FCSTD DOCUMENT  (FreeCAD 0.15R4671 (Git))
Label: TopCornerIdler_III
License: All rights reserved
LicenseURL: http://en.wikipedia.org/wiki/All_rights_reserved
objects: Sketcher::SketchObject×18, PartDesign::Pocket×17, PartDesign::Fillet×12, Part::Feature×11, Mesh::Feature×9, PartDesign::Pad×1
note: 77 computed .brp shape members not serialized (recipe doc carries the construction recipe); baked Part::Feature solids carry a one-line shape summary decoded from their .brp

FEATURE [Part::Feature] Part__Feature  label="OB1515_45mm001"
  Placement = pos=(0,-20.5,22.5) rot=(1,0,0;1.5708rad)
  shape: bbox 15 x 45 x 15 mm, 158 faces (baked)
FEATURE [Part::Feature] Part__Feature001  label="OB1515_45mm002"
  Placement = pos=(20.5,0,22.5) rot=(0.57735,0.57735,0.57735;2.0944rad)
  shape: bbox 45 x 15 x 15 mm, 158 faces (baked)
FEATURE [Part::Feature] Part__Feature002  label="OB1515_45mm"
  Placement = pos=(7,-7,-15) rot=(0,0,1;0.785398rad)
  shape: bbox 21.01 x 21.01 x 45 mm, 158 faces (baked)
FEATURE [Sketcher::SketchObject] Sketch
  Placement = pos=(0,0,2) rot=(0,0,1;0rad)
  sketch-geometry (5):
    g0: LineSegment StartX=-7.5 StartY=7.5 StartZ=0 EndX=62.0538 EndY=7.5 EndZ=0
    g1: LineSegment StartX=62.0538 StartY=7.5 StartZ=0 EndX=62.0538 EndY=-59.9462 EndZ=0
    g2: LineSegment StartX=62.0538 StartY=-59.9462 StartZ=0 EndX=52.5 EndY=-69.5 EndZ=0
    g3: LineSegment StartX=52.5 StartY=-69.5 StartZ=0 EndX=-7.5 EndY=-69.5 EndZ=0
    g4: LineSegment StartX=-7.5 StartY=-69.5 StartZ=0 EndX=-7.5 EndY=7.5 EndZ=0
  constraints (12):
    c: Coincident(g0,g1)
    c: Coincident(g1,g2)
    c: Coincident(g2,g3)
    c: Coincident(g3,g4)
    c: Coincident(g4,g0)
    c: Horizontal(g3)
    c: Horizontal(g0)
    c: Vertical(g1)
    c: Vertical(g4)
    c: Angle(g2,g-2) = 0.785398
    c: DistanceX(g0) = -7.5
    c: DistanceY(g0) = 7.5
FEATURE [Part::Feature] Part__Feature003  label="NEMA17"
  Placement = pos=(36,-36,2) rot=(0,0,1;0rad)
  shape: bbox 42.3 x 42.3 x 68 mm, 275 faces (baked)
FEATURE [Part::Feature] Part__Feature004  label="T5_Pulley"
  Placement = pos=(36,-36,-4) rot=(0,0,1;0rad)
  shape: bbox 16 x 16 x 14.8 mm, 116 faces (baked)
FEATURE [Mesh::Feature] _mmRod_x100mm  label="8mmRod_x100mm"
  Placement = pos=(36,-145.5,-3.5) rot=(0,0,1;3.14159rad)
FEATURE [Mesh::Feature] _08ZZ_Ball_Bearing  label="608ZZ_Ball_Bearing"
  Placement = pos=(54.5,-36,14) rot=(0,0,1;0rad)
FEATURE [Mesh::Feature] _08ZZ_Ball_Bearing001  label="608ZZ_Ball_Bearing001"
  Placement = pos=(54.5,-36,25.1) rot=(0,0,1;0rad)
FEATURE [Mesh::Feature] Spacer
  Placement = pos=(21.5,-46,17.6) rot=(0,0,1;0rad)
FEATURE [Part::Feature] LM8UU_8mm_Linear_Bearing
  Placement = pos=(36,-99.5,-3.5) rot=(0,0,1;1.5708rad)
  shape: bbox 15 x 24 x 15 mm, 34 faces (baked)
FEATURE [PartDesign::Pad] Pad
  Length = 28
  Length2 = 100
  Placement = pos=(0,0,2) rot=(0,0,1;0rad)
  Sketch = -> Sketch
  Type = 0
FEATURE [Sketcher::SketchObject] Sketch001
  Placement = pos=(0,0,30) rot=(0,0,1;0rad)
  Support = -> Pad [Face7]
  sketch-geometry (5):
    g0: LineSegment StartX=14.5 StartY=-73.368 StartZ=0 EndX=14.5 EndY=-19.8192 EndZ=0
    g1: LineSegment StartX=14.5 StartY=-19.8192 StartZ=0 EndX=19.8192 EndY=-14.5 EndZ=0
    g2: LineSegment StartX=19.8192 StartY=-14.5 StartZ=0 EndX=77 EndY=-14.5 EndZ=0
    g3: LineSegment StartX=77 StartY=-14.5 StartZ=0 EndX=77 EndY=-73.368 EndZ=0
    g4: LineSegment StartX=77 StartY=-73.368 StartZ=0 EndX=14.5 EndY=-73.368 EndZ=0
  constraints (12):
    c: Coincident(g0,g1)
    c: Coincident(g1,g2)
    c: Coincident(g2,g3)
    c: Coincident(g3,g4)
    c: Coincident(g0,g4)
    c: Horizontal(g4)
    c: Horizontal(g2)
    c: Vertical(g0)
    c: Vertical(g3)
    c: Angle(g1,g-2) = 0.785398
    c: DistanceY(g-1,g2) = -14.5
    c: DistanceX(g-1,g0) = 14.5
FEATURE [PartDesign::Pocket] Pocket
  Length = 21
  Placement = pos=(0,0,2) rot=(0,0,1;0rad)
  Sketch = -> Sketch001
  Type = 0
FEATURE [Sketcher::SketchObject] Sketch002
  Placement = pos=(0,0,30) rot=(0,0,1;0rad)
  Support = -> Pocket [Face5]
  sketch-geometry (8):
    g0: LineSegment StartX=-8 StartY=-20.5 StartZ=0 EndX=7.5 EndY=-20.5 EndZ=0
    g1: LineSegment StartX=7.5 StartY=-20.5 StartZ=0 EndX=7.5 EndY=-71.5 EndZ=0
    g2: LineSegment StartX=7.5 StartY=-71.5 StartZ=0 EndX=-8 EndY=-71.5 EndZ=0
    g3: LineSegment StartX=-8 StartY=-71.5 StartZ=0 EndX=-8 EndY=-20.5 EndZ=0
    g4: LineSegment StartX=20.5 StartY=8 StartZ=0 EndX=76.5 EndY=8 EndZ=0
    g5: LineSegment StartX=76.5 StartY=8 StartZ=0 EndX=76.5 EndY=-7.5 EndZ=0
    g6: LineSegment StartX=76.5 StartY=-7.5 StartZ=0 EndX=20.5 EndY=-7.5 EndZ=0
    g7: LineSegment StartX=20.5 StartY=-7.5 StartZ=0 EndX=20.5 EndY=8 EndZ=0
  constraints (16):
    c: Coincident(g0,g1)
    c: Coincident(g1,g2)
    c: Coincident(g2,g3)
    c: Coincident(g3,g0)
    c: Horizontal(g0)
    c: Horizontal(g2)
    c: Vertical(g1)
    c: Vertical(g3)
    c: Coincident(g4,g5)
    c: Coincident(g5,g6)
    c: Coincident(g6,g7)
    c: Coincident(g7,g4)
    c: Horizontal(g4)
    c: Horizontal(g6)
    c: Vertical(g5)
    c: Vertical(g7)
FEATURE [PartDesign::Pocket] Pocket001
  Length = 15
  Placement = pos=(0,0,2) rot=(0,0,1;0rad)
  Sketch = -> Sketch002
  Type = 0
FEATURE [Sketcher::SketchObject] Sketch003
  Placement = pos=(0,0,30) rot=(0,0,1;0rad)
  Support = -> Pocket001 [Face6]
  sketch-geometry (4):
    g0: LineSegment StartX=7 StartY=4 StartZ=0 EndX=18 EndY=-7 EndZ=0
    g1: LineSegment StartX=18 StartY=-7 StartZ=0 EndX=7 EndY=-18 EndZ=0
    g2: LineSegment StartX=7 StartY=-18 StartZ=0 EndX=-4 EndY=-7 EndZ=0
    g3: LineSegment StartX=-4 StartY=-7 StartZ=0 EndX=7 EndY=4 EndZ=0
  constraints (4):
    c: Coincident(g0,g1)
    c: Coincident(g1,g2)
    c: Coincident(g2,g3)
    c: Coincident(g3,g0)
FEATURE [PartDesign::Pocket] Pocket002
  Length = 5
  Placement = pos=(0,0,2) rot=(0,0,1;0rad)
  Sketch = -> Sketch003
  Type = 1
FEATURE [Sketcher::SketchObject] Sketch004
  Placement = pos=(0,0,30) rot=(0,0,1;0rad)
  Support = -> Pocket002 [Face6]
  sketch-geometry (5):
    g0: LineSegment StartX=-8 StartY=-1 StartZ=0 EndX=-7.5 EndY=-1 EndZ=0
    g1: LineSegment StartX=-7.5 StartY=-1 StartZ=0 EndX=1 EndY=7.6037 EndZ=0
    g2: LineSegment StartX=1 StartY=7.6037 StartZ=0 EndX=1 EndY=8 EndZ=0
    g3: LineSegment StartX=1 StartY=8 StartZ=0 EndX=-8 EndY=8 EndZ=0
    g4: LineSegment StartX=-8 StartY=8 StartZ=0 EndX=-8 EndY=-1 EndZ=0
  constraints (7):
    c: Coincident(g0,g1)
    c: Coincident(g1,g2)
    c: Coincident(g2,g3)
    c: Coincident(g3,g4)
    c: Coincident(g4,g0)
    c: Vertical(g2)
    c: Horizontal(g0)
FEATURE [PartDesign::Pocket] Pocket003
  Length = 5
  Placement = pos=(0,0,2) rot=(0,0,1;0rad)
  Sketch = -> Sketch004
  Type = 1
FEATURE [Mesh::Feature] tempTopCornerCap
  Placement = pos=(0,0,-7) rot=(0,0,1;0rad)
FEATURE [PartDesign::Fillet] Fillet
  Base = -> Pocket003 [Edge16,Edge40]
  Placement = pos=(0,0,2) rot=(0,0,1;0rad)
  Radius = 4
FEATURE [PartDesign::Fillet] Fillet001
  Base = -> Fillet [Edge29,Edge25]
  Placement = pos=(0,0,2) rot=(0,0,1;0rad)
  Radius = 4
FEATURE [Sketcher::SketchObject] Sketch005
  Placement = pos=(0,0,2) rot=(1,0,0;3.14159rad)
  Support = -> Fillet001 [Face1]
  sketch-geometry (4):
    g0: Circle CenterX=0 CenterY=60 CenterZ=0 NormalX=0 NormalY=0 NormalZ=1 Radius=1.8
    g1: Circle CenterX=0 CenterY=25 CenterZ=0 NormalX=0 NormalY=0 NormalZ=1 Radius=1.8
    g2: Circle CenterX=57.5 CenterY=0 CenterZ=0 NormalX=0 NormalY=0 NormalZ=1 Radius=1.8
    g3: Circle CenterX=25 CenterY=0 CenterZ=0 NormalX=0 NormalY=0 NormalZ=1 Radius=1.8
  constraints (4):
    c: Radius(g2) = 1.8
    c: Radius(g3) = 1.8
    c: Radius(g1) = 1.8
    c: Radius(g0) = 1.8
FEATURE [PartDesign::Pocket] Pocket004
  Length = 5
  Placement = pos=(0,0,2) rot=(0,0,1;0rad)
  Sketch = -> Sketch005
  Type = 1
FEATURE [Sketcher::SketchObject] Sketch006
  Placement = pos=(0,0,2) rot=(1,0,0;3.14159rad)
  Support = -> Pocket004 [Face1]
  sketch-geometry (4):
    g0: Circle CenterX=57.5 CenterY=0 CenterZ=0 NormalX=0 NormalY=0 NormalZ=1 Radius=3.6
    g1: Circle CenterX=25 CenterY=0 CenterZ=0 NormalX=0 NormalY=0 NormalZ=1 Radius=3.6
    g2: Circle CenterX=0 CenterY=25 CenterZ=0 NormalX=0 NormalY=0 NormalZ=1 Radius=3.6
    g3: Circle CenterX=0 CenterY=60 CenterZ=0 NormalX=0 NormalY=0 NormalZ=1 Radius=3.6
  constraints (4):
    c: Radius(g3) = 3.6
    c: Radius(g2) = 3.6
    c: Radius(g1) = 3.6
    c: Radius(g0) = 3.6
FEATURE [PartDesign::Pocket] Pocket005
  Length = 9
  Placement = pos=(0,0,2) rot=(0,0,1;0rad)
  Sketch = -> Sketch006
  Type = 0
FEATURE [Sketcher::SketchObject] Sketch007
  Placement = pos=(14.5,0,2) rot=(0.57735,0.57735,0.57735;2.0944rad)
  Support = -> Pocket005 [Face28]
  sketch-geometry (2):
    g0: Circle CenterX=-25 CenterY=20.5 CenterZ=0 NormalX=0 NormalY=0 NormalZ=1 Radius=1.8
    g1: Circle CenterX=-60 CenterY=20.5 CenterZ=0 NormalX=0 NormalY=0 NormalZ=1 Radius=1.8
  constraints (2):
    c: Radius(g0) = 1.8
    c: Radius(g1) = 1.8
FEATURE [PartDesign::Pocket] Pocket006
  Length = 5
  Placement = pos=(0,0,2) rot=(0,0,1;0rad)
  Sketch = -> Sketch007
  Type = 1
FEATURE [Sketcher::SketchObject] Sketch008
  Placement = pos=(14.5,0,2) rot=(0.57735,0.57735,0.57735;2.0944rad)
  Support = -> Pocket006 [Face28]
  sketch-geometry (2):
    g0: Circle CenterX=-25 CenterY=20.5 CenterZ=0 NormalX=0 NormalY=0 NormalZ=1 Radius=3.6
    g1: Circle CenterX=-60 CenterY=20.5 CenterZ=0 NormalX=0 NormalY=0 NormalZ=1 Radius=3.6
  constraints (2):
    c: Radius(g1) = 3.6
    c: Radius(g0) = 3.6
FEATURE [PartDesign::Pocket] Pocket007
  Length = 3
  Placement = pos=(0,0,2) rot=(0,0,1;0rad)
  Sketch = -> Sketch008
  Type = 0
FEATURE [Sketcher::SketchObject] Sketch009
  Placement = pos=(0,-14.5,2) rot=(1,0,0;1.5708rad)
  Support = -> Pocket007 [Face24]
  sketch-geometry (2):
    g0: Circle CenterX=25 CenterY=20.5 CenterZ=0 NormalX=0 NormalY=0 NormalZ=1 Radius=1.8
    g1: Circle CenterX=57.5 CenterY=20.5 CenterZ=0 NormalX=0 NormalY=0 NormalZ=1 Radius=1.8
  constraints (2):
    c: Radius(g0) = 1.8
    c: Radius(g1) = 1.8
FEATURE [PartDesign::Pocket] Pocket008
  Length = 5
  Placement = pos=(0,0,2) rot=(0,0,1;0rad)
  Sketch = -> Sketch009
  Type = 1
FEATURE [Sketcher::SketchObject] Sketch010
  Placement = pos=(0,-14.5,2) rot=(1,0,0;1.5708rad)
  Support = -> Pocket008 [Face24]
  sketch-geometry (2):
    g0: Circle CenterX=57.5 CenterY=20.5 CenterZ=0 NormalX=0 NormalY=0 NormalZ=1 Radius=3.6
    g1: Circle CenterX=25 CenterY=20.5 CenterZ=0 NormalX=0 NormalY=0 NormalZ=1 Radius=3.6
  constraints (2):
    c: Radius(g1) = 3.6
    c: Radius(g0) = 3.6
FEATURE [PartDesign::Pocket] Pocket009
  Length = 3
  Placement = pos=(0,0,2) rot=(0,0,1;0rad)
  Sketch = -> Sketch010
  Type = 0
FEATURE [PartDesign::Fillet] Fillet002
  Base = -> Pocket009 [Edge92,Edge82]
  Placement = pos=(0,0,2) rot=(0,0,1;0rad)
  Radius = 2
FEATURE [PartDesign::Fillet] Fillet003
  Base = -> Fillet002 [Edge45,Edge35,Edge23]
  Placement = pos=(0,0,2) rot=(0,0,1;0rad)
  Radius = 2
FEATURE [Part::Feature] Fillet003001  label="TopCornerMaster_NoRodHolder"
  shape: bbox 69.55 x 77 x 28 mm, 57 faces (baked)
FEATURE [Part::Feature] Part__Feature005  label="TopRodHolder"
  Placement = pos=(0,0,2) rot=(0,0,1;0rad)
  shape: bbox 30.16 x 11.33 x 11.99 mm, 56 faces (baked)
FEATURE [Sketcher::SketchObject] Sketch011
  Placement = pos=(0,0,9) rot=(0,0,1;0rad)
  Support = -> Fillet003001 [Face10]
  sketch-geometry (2):
    g0: Circle CenterX=25 CenterY=-64 CenterZ=0 NormalX=0 NormalY=0 NormalZ=1 Radius=1.8
    g1: Circle CenterX=47 CenterY=-64 CenterZ=0 NormalX=0 NormalY=0 NormalZ=1 Radius=1.8
  constraints (2):
    c: Radius(g0) = 1.8
    c: Radius(g1) = 1.8
FEATURE [PartDesign::Pocket] Pocket010
  Length = 5
  Sketch = -> Sketch011
  Type = 1
FEATURE [Sketcher::SketchObject] Sketch012
  Placement = pos=(0,0,9) rot=(0,0,1;0rad)
  Support = -> Pocket010 [Face10]
  sketch-geometry (2):
    g0: Circle CenterX=25 CenterY=-64 CenterZ=0 NormalX=0 NormalY=0 NormalZ=1 Radius=3.6
    g1: Circle CenterX=47 CenterY=-64 CenterZ=0 NormalX=0 NormalY=0 NormalZ=1 Radius=3.6
  constraints (2):
    c: Radius(g0) = 3.6
    c: Radius(g1) = 3.6
FEATURE [PartDesign::Pocket] Pocket011  label="TopCornerMaster"
  Length = 3
  Sketch = -> Sketch012
  Type = 0
FEATURE [Mesh::Feature] _x10x4_FlangedBearing  label="5x10x4_FlangedBearing_B"
  Placement = pos=(48,-46,12) rot=(1,0,0;1.5708rad)
FEATURE [Mesh::Feature] _x10x4_FlangedBearing001  label="5x10x4_FlangedBearing_T"
  Placement = pos=(48,-46,16) rot=(-1,0,0;1.5708rad)
FEATURE [Mesh::Feature] _x10x4_FlangedBearing002  label="5x10x4_FlangedBearing_B001"
  Placement = pos=(35,-31,23) rot=(1,0,0;1.5708rad)
FEATURE [Mesh::Feature] _x10x4_FlangedBearing003  label="5x10x4_FlangedBearing_T001"
  Placement = pos=(35,-31,27) rot=(-1,0,0;1.5708rad)
FEATURE [Sketcher::SketchObject] Sketch013
  Placement = pos=(0,0,9) rot=(0,0,1;0rad)
  Support = -> Pocket011 [Face10]
  sketch-geometry (2):
    g0: Circle CenterX=35 CenterY=-31 CenterZ=0 NormalX=0 NormalY=0 NormalZ=1 Radius=1.8
    g1: Circle CenterX=48 CenterY=-46 CenterZ=0 NormalX=0 NormalY=0 NormalZ=1 Radius=1.8
  constraints (2):
    c: Radius(g0) = 1.8
    c: Equal(g0,g1)
FEATURE [PartDesign::Pocket] Pocket012  label="TopCornerIdler_II"
  Length = 5
  Sketch = -> Sketch013
  Type = 0
FEATURE [Part::Feature] Part__Feature006  label="IdlerBearingStandoff"
  Placement = pos=(48,-46,19) rot=(0,0,1;0rad)
  shape: bbox 6 x 6 x 11 mm, 4 faces (baked)
FEATURE [Part::Feature] Part__Feature007  label="IdlerBearingStandoff001"
  Placement = pos=(35,-31,9) rot=(0,0,1;0rad)
  shape: bbox 6 x 6 x 11 mm, 4 faces (baked)
FEATURE [Part::Feature] Part__Feature008  label="TopCornerCapIdler_II"
  Placement = pos=(0,0,28) rot=(0,0,1;0rad)
  shape: bbox 69.55 x 77 x 7 mm, 28 faces (baked)
FEATURE [Sketcher::SketchObject] Sketch014
  Placement = pos=(-3.29551,3.25579,0) rot=(-0.283305,0.678137,0.678137;3.69373rad)
  Support = -> Pocket012 [Face19]
  sketch-geometry (2):
    g0: Circle CenterX=0 CenterY=25 CenterZ=0 NormalX=0 NormalY=0 NormalZ=1 Radius=1.8
    g1: Circle CenterX=0 CenterY=7.5 CenterZ=0 NormalX=0 NormalY=0 NormalZ=1 Radius=1.8
  constraints (2):
    c: Radius(g0) = 1.8
    c: Equal(g0,g1)
FEATURE [PartDesign::Pocket] Pocket013
  Length = 12
  Sketch = -> Sketch014
  Type = 0
FEATURE [Sketcher::SketchObject] Sketch015
  Placement = pos=(-3.29551,3.25579,0) rot=(-0.283305,0.678137,0.678137;3.69373rad)
  Support = -> Pocket013 [Face19]
  sketch-geometry (2):
    g0: Circle CenterX=0 CenterY=25 CenterZ=0 NormalX=0 NormalY=0 NormalZ=1 Radius=3.6
    g1: Circle CenterX=0 CenterY=7.5 CenterZ=0 NormalX=0 NormalY=0 NormalZ=1 Radius=3.6
  constraints (2):
    c: Radius(g0) = 3.6
    c: Equal(g0,g1)
FEATURE [PartDesign::Pocket] Pocket014  label="TopCorneIdler_II"
  Length = 3
  Sketch = -> Sketch015
  Type = 0
FEATURE [Sketcher::SketchObject] Sketch016
  Placement = pos=(0,0,2) rot=(1,0,0;3.14159rad)
  Support = -> Pocket014 [Face28]
  sketch-geometry (14):
    g0: LineSegment StartX=-5 StartY=54 StartZ=0 EndX=5 EndY=54 EndZ=0
    g1: LineSegment StartX=5 StartY=54 StartZ=0 EndX=5 EndY=31 EndZ=0
    g2: LineSegment StartX=5 StartY=31 StartZ=0 EndX=-5 EndY=31 EndZ=0
    g3: LineSegment StartX=-5 StartY=31 StartZ=0 EndX=-5 EndY=54 EndZ=0
    g4: LineSegment StartX=31 StartY=5 StartZ=0 EndX=52 EndY=5 EndZ=0
    g5: LineSegment StartX=52 StartY=5 StartZ=0 EndX=52 EndY=-5 EndZ=0
    g6: LineSegment StartX=52 StartY=-5 StartZ=0 EndX=31 EndY=-5 EndZ=0
    g7: LineSegment StartX=31 StartY=-5 StartZ=0 EndX=31 EndY=5 EndZ=0
    g8: LineSegment StartX=19 StartY=5 StartZ=0 EndX=19 EndY=-5 EndZ=0
    g9: LineSegment StartX=19 StartY=-5 StartZ=0 EndX=9 EndY=-5 EndZ=0
    g10: LineSegment StartX=9 StartY=-5 StartZ=0 EndX=19 EndY=5 EndZ=0
    g11: LineSegment StartX=-5 StartY=19 StartZ=0 EndX=5 EndY=19 EndZ=0
    g12: LineSegment StartX=5 StartY=19 StartZ=0 EndX=-5 EndY=10 EndZ=0
    g13: LineSegment StartX=-5 StartY=10 StartZ=0 EndX=-5 EndY=19 EndZ=0
  constraints (22):
    c: Coincident(g0,g1)
    c: Coincident(g1,g2)
    c: Coincident(g2,g3)
    c: Coincident(g3,g0)
    c: Horizontal(g0)
    c: Horizontal(g2)
    c: Vertical(g1)
    c: Vertical(g3)
    c: Coincident(g4,g5)
    c: Coincident(g5,g6)
    c: Coincident(g6,g7)
    c: Coincident(g7,g4)
    c: Horizontal(g4)
    c: Horizontal(g6)
    c: Vertical(g5)
    c: Vertical(g7)
    c: Coincident(g8,g9)
    c: Coincident(g9,g10)
    c: Coincident(g10,g8)
    c: Coincident(g11,g12)
    c: Coincident(g12,g13)
    c: Coincident(g13,g11)
FEATURE [PartDesign::Pocket] Pocket015
  Length = 5
  Sketch = -> Sketch016
  Type = 1
FEATURE [Sketcher::SketchObject] Sketch017
  Placement = pos=(0,0,9) rot=(0,0,1;0rad)
  Support = -> Pocket015 [Face10]
  sketch-geometry (12):
    g0: LineSegment StartX=59 StartY=-19 StartZ=0 EndX=22 EndY=-19 EndZ=0
    g1: LineSegment StartX=22 StartY=-19 StartZ=0 EndX=19 EndY=-22 EndZ=0
    g2: LineSegment StartX=19 StartY=-22 StartZ=0 EndX=19 EndY=-58 EndZ=0
    g3: ArcOfCircle CenterX=25 CenterY=-64 CenterZ=0 NormalX=0 NormalY=0 NormalZ=1 Radius=6 StartAngle=0 EndAngle=1.5708
    g4: ArcOfCircle CenterX=47 CenterY=-64 CenterZ=0 NormalX=0 NormalY=0 NormalZ=1 Radius=6 StartAngle=6.28319 EndAngle=9.42478
    g5: LineSegment StartX=25 StartY=-58 StartZ=0 EndX=19 EndY=-58 EndZ=0
    g6: LineSegment StartX=31 StartY=-64 StartZ=0 EndX=41 EndY=-64 EndZ=0
    g7: LineSegment StartX=53 StartY=-64 StartZ=0 EndX=54 EndY=-64 EndZ=0
    g8: LineSegment StartX=54 StartY=-64 StartZ=0 EndX=59 EndY=-59 EndZ=0
    g9: LineSegment StartX=59 StartY=-59 StartZ=0 EndX=59 EndY=-19 EndZ=0
    g10: Circle CenterX=35 CenterY=-31 CenterZ=0 NormalX=0 NormalY=0 NormalZ=1 Radius=5
    g11: Circle CenterX=48 CenterY=-46 CenterZ=0 NormalX=0 NormalY=0 NormalZ=1 Radius=5
  constraints (10):
    c: Coincident(g0,g1)
    c: Coincident(g1,g2)
    c: Coincident(g7,g8)
    c: Coincident(g8,g9)
    c: Coincident(g0,g9)
    c: Coincident(g3,g6)
    c: Coincident(g3,g5)
    c: Coincident(g2,g5)
    c: Coincident(g4,g7)
    c: Coincident(g4,g6)
FEATURE [PartDesign::Pocket] Pocket016
  Length = 4
  Sketch = -> Sketch017
  Type = 0
FEATURE [PartDesign::Fillet] Fillet003002
  Base = -> Pocket016 [Edge167,Edge165,Edge163,Edge161,Edge159]
  Radius = 2
FEATURE [PartDesign::Fillet] Fillet003003
  Base = -> Fillet003002 [Edge39,Edge36,Edge31,Edge27]
  Radius = 0.5
FEATURE [PartDesign::Fillet] Fillet003004
  Base = -> Fillet003003 [Edge16]
  Radius = 1
FEATURE [PartDesign::Fillet] Fillet003005
  Base = -> Fillet003004 [Edge293,Edge295,Edge234,Edge233]
  Radius = 1
FEATURE [PartDesign::Fillet] Fillet003006
  Base = -> Fillet003005 [Edge9]
  Radius = 1
FEATURE [PartDesign::Fillet] Fillet003007
  Base = -> Fillet003006 [Edge314,Edge316,Edge315,Edge306,Edge307,Edge305]
  Radius = 1.5
FEATURE [PartDesign::Fillet] Fillet003008
  Base = -> Fillet003007 [Edge91,Edge114,Edge92,Edge113,Edge94,Edge111,Edge89,Edge116]
  Radius = 2
FEATURE [PartDesign::Fillet] Fillet003009
  Base = -> Fillet003008 [Edge16]
  Radius = 2
